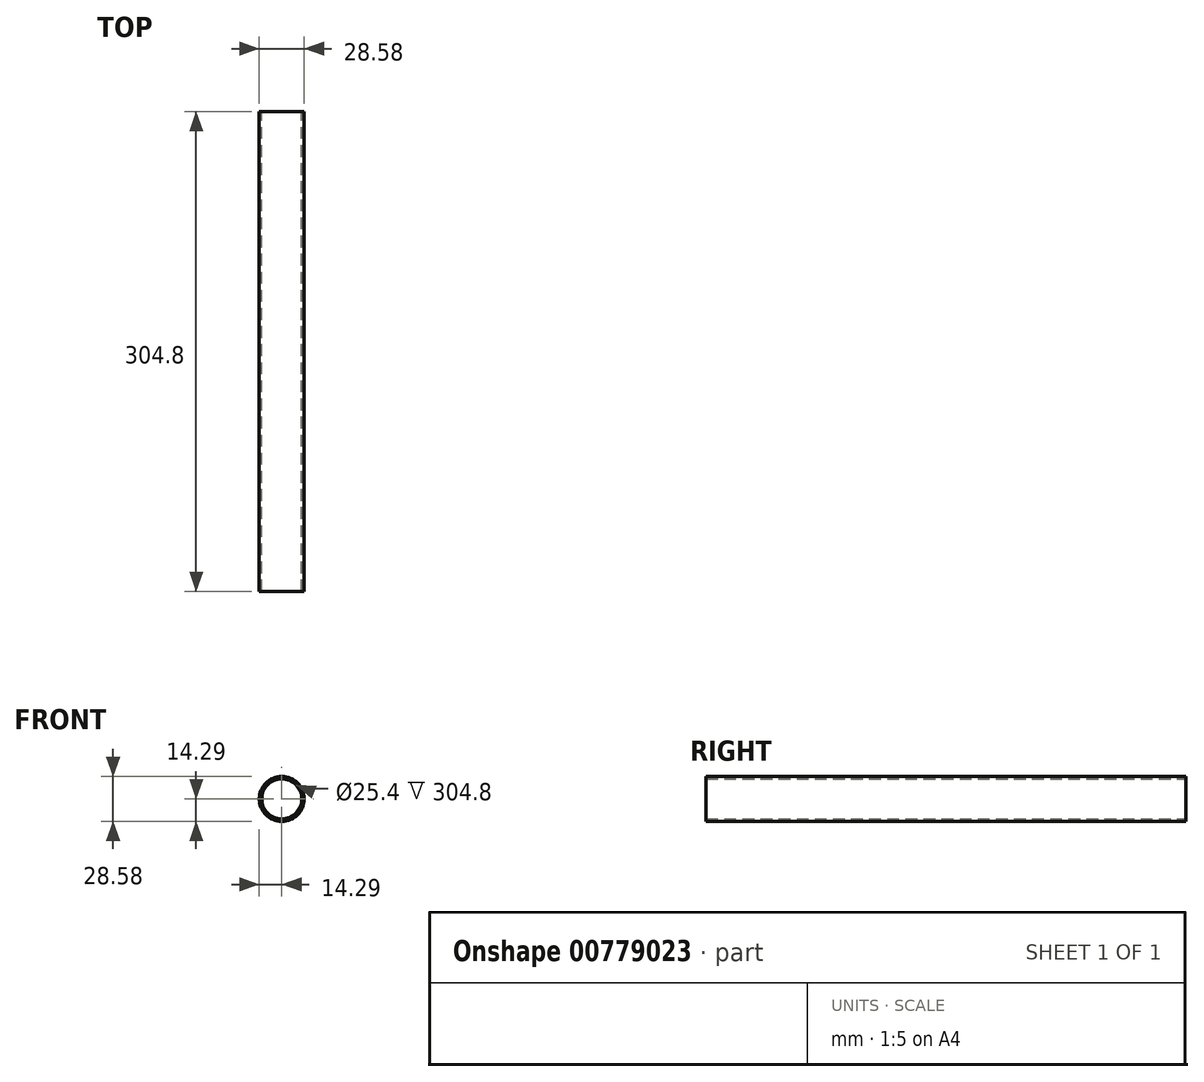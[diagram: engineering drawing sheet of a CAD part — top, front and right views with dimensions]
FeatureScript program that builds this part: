
annotation { "Feature Type Name" : "Feature", "Feature Type Description" : "" }
export const myFeature = defineFeature(function(context is Context, id is Id, definition is map)
    precondition{}
    {
        {
            var Q0;
            Q0=qCreatedBy(makeId("Front.planeOp"),FACE);
            var sketch = newSketch(context, id + "F0", { "sketchPlane" : qUnion([Q0])});
            skCircle(sketch, "E0", {"center": v(0, 0) * mm, "radius": 14.29 * mm});
            skCircle(sketch, "E1", {"center": v(0, 0) * mm, "radius": 12.7 * mm});
            skSolve(sketch);
        }
        {
            var Q0;
            Q0 = qSketchRegion(id + "F0", true);
            extrude(context, id + "F1", {"entities" : qUnion([Q0]), "depth" : 304.8 * mm, "offsetDistance" : 25.4 * mm});
        }
    });
